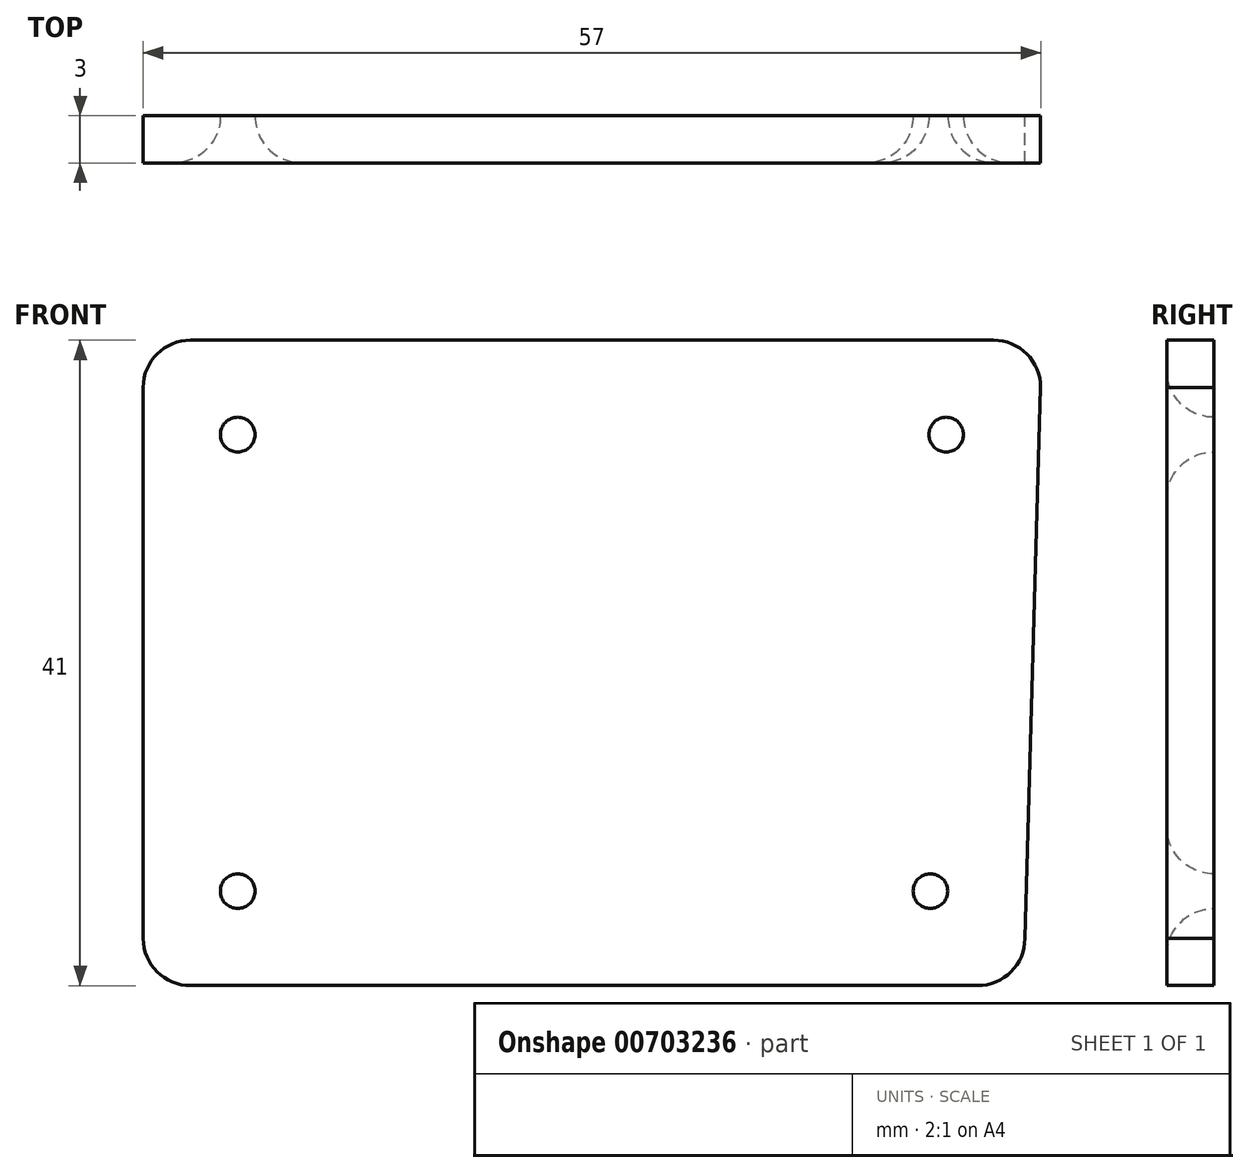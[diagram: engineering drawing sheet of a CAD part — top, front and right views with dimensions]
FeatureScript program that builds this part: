
annotation { "Feature Type Name" : "Feature", "Feature Type Description" : "" }
export const myFeature = defineFeature(function(context is Context, id is Id, definition is map)
    precondition{}
    {
        {
            var Q0;
            Q0=qCreatedBy(makeId("Front.planeOp"),FACE);
            var sketch = newSketch(context, id + "F0", { "sketchPlane" : qUnion([Q0])});
            skLineSegment(sketch, "E0", {"start": v(-25.48, -6.75) * mm, "end": v(-21.93, -6.75) * mm});
            skLineSegment(sketch, "E1", {"start": v(-21.93, -6.75) * mm, "end": v(-21.93, -4.75) * mm});
            skLineSegment(sketch, "E2", {"start": v(-21.93, -4.75) * mm, "end": v(-25.48, -4.75) * mm});
            skLineSegment(sketch, "E3", {"start": v(-25.48, -4.75) * mm, "end": v(-25.48, -2.75) * mm});
            skLineSegment(sketch, "E4", {"start": v(-25.48, -2.75) * mm, "end": v(-21.8, -2.75) * mm});
            skLineSegment(sketch, "E5", {"start": v(-21.8, -2.75) * mm, "end": v(-21.8, -0.75) * mm});
            skLineSegment(sketch, "E6", {"start": v(-21.8, -0.75) * mm, "end": v(-25.48, -0.75) * mm});
            skLineSegment(sketch, "E7", {"start": v(24.52, -0.75) * mm, "end": v(20.83, -0.75) * mm});
            skLineSegment(sketch, "E8", {"start": v(20.83, -0.75) * mm, "end": v(20.83, -2.75) * mm});
            skLineSegment(sketch, "E9", {"start": v(20.83, -2.75) * mm, "end": v(24.52, -2.75) * mm});
            skLineSegment(sketch, "E10", {"start": v(24.52, -2.75) * mm, "end": v(24.52, -4.75) * mm});
            skLineSegment(sketch, "E11", {"start": v(24.52, -4.75) * mm, "end": v(20.8, -4.75) * mm});
            skLineSegment(sketch, "E12", {"start": v(20.8, -4.75) * mm, "end": v(20.8, -6.75) * mm});
            skLineSegment(sketch, "E13", {"start": v(20.8, -6.75) * mm, "end": v(24.52, -6.75) * mm});
            skLineSegment(sketch, "E14", {"start": v(24.52, -6.75) * mm, "end": v(24.52, -14.75) * mm});
            skLineSegment(sketch, "E15.bottom", {"start": v(-25.48, 20.25) * mm, "end": v(-19.48, 20.25) * mm});
            skLineSegment(sketch, "E15.top", {"start": v(-25.48, 14.25) * mm, "end": v(-19.48, 14.25) * mm});
            skLineSegment(sketch, "E15.left", {"start": v(-25.48, 20.25) * mm, "end": v(-25.48, 14.25) * mm});
            skLineSegment(sketch, "E15.right", {"start": v(-19.48, 20.25) * mm, "end": v(-19.48, 14.25) * mm});
            skLineSegment(sketch, "E16.bottom", {"start": v(25.52, 20.25) * mm, "end": v(19.52, 20.25) * mm});
            skLineSegment(sketch, "E16.top", {"start": v(25.52, 14.25) * mm, "end": v(19.52, 14.25) * mm});
            skLineSegment(sketch, "E16.left", {"start": v(25.52, 20.25) * mm, "end": v(25.52, 14.25) * mm});
            skLineSegment(sketch, "E16.right", {"start": v(19.52, 20.25) * mm, "end": v(19.52, 14.25) * mm});
            skLineSegment(sketch, "E17.bottom", {"start": v(24.52, -14.75) * mm, "end": v(18.52, -14.75) * mm});
            skLineSegment(sketch, "E17.top", {"start": v(24.52, -8.75) * mm, "end": v(18.52, -8.75) * mm});
            skLineSegment(sketch, "E17.left", {"start": v(24.52, -14.75) * mm, "end": v(24.52, -8.75) * mm});
            skLineSegment(sketch, "E17.right", {"start": v(18.52, -14.75) * mm, "end": v(18.52, -8.75) * mm});
            skLineSegment(sketch, "E18.bottom", {"start": v(-25.48, -14.75) * mm, "end": v(-19.48, -14.75) * mm});
            skLineSegment(sketch, "E18.top", {"start": v(-25.48, -8.75) * mm, "end": v(-19.48, -8.75) * mm});
            skLineSegment(sketch, "E18.left", {"start": v(-25.48, -14.75) * mm, "end": v(-25.48, -8.75) * mm});
            skLineSegment(sketch, "E18.right", {"start": v(-19.48, -14.75) * mm, "end": v(-19.48, -8.75) * mm});
            skLineSegment(sketch, "E19.bottom", {"start": v(-25.48, -14.75) * mm, "end": v(25.52, -14.75) * mm});
            skLineSegment(sketch, "E19.top", {"start": v(-25.48, 20.25) * mm, "end": v(25.52, 20.25) * mm});
            skLineSegment(sketch, "E19.left", {"start": v(-25.48, -14.75) * mm, "end": v(-25.48, 20.25) * mm});
            skLineSegment(sketch, "E19.right", {"start": v(25.52, -14.75) * mm, "end": v(25.52, 20.25) * mm});
            skLineSegment(sketch, "E20.top", {"start": v(-25.48, -0.75) * mm, "end": v(-21.8, -0.75) * mm});
            skLineSegment(sketch, "E20.left", {"start": v(-25.48, -2.75) * mm, "end": v(-25.48, -0.75) * mm});
            skLineSegment(sketch, "E21.top", {"start": v(20.83, -0.75) * mm, "end": v(24.52, -0.75) * mm});
            skLineSegment(sketch, "E21.left", {"start": v(20.83, -2.75) * mm, "end": v(20.83, -0.75) * mm});
            skLineSegment(sketch, "E21.right", {"start": v(24.52, -2.75) * mm, "end": v(24.52, -0.75) * mm});
            skArc(sketch, "E22", {"start": v(-25.48, 23.25) * mm, "mid": v(-27.6, 22.38) * mm, "end": v(-28.48, 20.25) * mm});
            skArc(sketch, "E23", {"start": v(-25.48, -17.75) * mm, "mid": v(-27.6, -16.87) * mm, "end": v(-28.48, -14.75) * mm});
            skArc(sketch, "E24", {"start": v(24.52, -17.75) * mm, "mid": v(26.64, -16.87) * mm, "end": v(27.52, -14.75) * mm});
            skArc(sketch, "E25", {"start": v(25.52, 23.25) * mm, "mid": v(27.64, 22.38) * mm, "end": v(28.52, 20.25) * mm});
            skLineSegment(sketch, "E26", {"start": v(-28.48, -14.75) * mm, "end": v(-28.48, 20.25) * mm});
            skLineSegment(sketch, "E27", {"start": v(27.52, -14.75) * mm, "end": v(28.52, 20.25) * mm});
            skLineSegment(sketch, "E28", {"start": v(-25.48, -17.75) * mm, "end": v(24.52, -17.75) * mm});
            skLineSegment(sketch, "E29", {"start": v(25.52, 23.25) * mm, "end": v(-25.48, 23.25) * mm});
            skCircle(sketch, "E30", {"center": v(-22.48, -11.75) * mm, "radius": 1.1 * mm});
            skPoint(sketch, "E30.centerSnap0", {"position": v(-19.48, -11.75) * mm});
            skPoint(sketch, "E30.centerSnap1", {"position": v(-22.48, -14.75) * mm});
            skCircle(sketch, "E31", {"center": v(-22.48, 17.25) * mm, "radius": 1.1 * mm});
            skPoint(sketch, "E31.centerSnap0", {"position": v(-19.48, 17.25) * mm});
            skPoint(sketch, "E31.centerSnap1", {"position": v(-22.48, 14.25) * mm});
            skCircle(sketch, "E32", {"center": v(22.52, 17.25) * mm, "radius": 1.1 * mm});
            skPoint(sketch, "E32.centerSnap0", {"position": v(19.52, 17.25) * mm});
            skPoint(sketch, "E32.centerSnap1", {"position": v(22.52, 14.25) * mm});
            skCircle(sketch, "E33", {"center": v(21.52, -11.75) * mm, "radius": 1.1 * mm});
            skPoint(sketch, "E33.centerSnap0", {"position": v(21.52, -8.75) * mm});
            skPoint(sketch, "E33.centerSnap1", {"position": v(18.52, -11.75) * mm});
            skSolve(sketch);
        }
        {
            var Q0;
            Q0=makeQuery(id+"F0.imprint","IMPRINT",FACE,{"disambiguationData":[TD([[makeQuery(id+"F0.imprint","IMPRINT",EDGE,{"derivedFrom":sQuery(id+"F0.wireOp",EDGE,"E16.bottom")}),1.0]])]});
            var Q1;
            {var subQ2=sQuery(id+"F0.wireOp",EDGE,"E3");Q1=makeQuery(id+"F0.imprint","IMPRINT",FACE,{"disambiguationData":[TD([[makeQuery(id+"F0.imprint","IMPRINT",EDGE,{"derivedFrom":subQ2}),1.0]])]});}
            var Q2;
            Q2=makeQuery(id+"F0.imprint","IMPRINT",FACE,{"disambiguationData":[TD([[makeQuery(id+"F0.imprint","IMPRINT",EDGE,{"derivedFrom":sQuery(id+"F0.wireOp",EDGE,"E15.bottom")}),-1.0]])]});
            var Q3;
            {var subQ0=sQuery(id+"F0.wireOp",EDGE,"E0");Q3=makeQuery(id+"F0.imprint","IMPRINT",FACE,{"disambiguationData":[TD([[makeQuery(id+"F0.imprint","IMPRINT",EDGE,{"derivedFrom":subQ0}),1.0]])]});}
            var Q4;
            {var subQ9=sQuery(id+"F0.wireOp",EDGE,"E0");Q4=makeQuery(id+"F0.imprint","IMPRINT",FACE,{"disambiguationData":[TD([[makeQuery(id+"F0.imprint","IMPRINT",EDGE,{"derivedFrom":subQ9}),-1.0]])]});}
            var Q5;
            {var subQ0=sQuery(id+"F0.wireOp",EDGE,"E4");Q5=makeQuery(id+"F0.imprint","IMPRINT",FACE,{"disambiguationData":[TD([[makeQuery(id+"F0.imprint","IMPRINT",EDGE,{"derivedFrom":subQ0}),1.0]])]});}
            var Q6;
            Q6=makeQuery(id+"F0.imprint","IMPRINT",FACE,{"disambiguationData":[TD([[makeQuery(id+"F0.imprint","IMPRINT",EDGE,{"derivedFrom":sQuery(id+"F0.wireOp",EDGE,"E7")}),1.0]])]});
            var Q7;
            Q7=makeQuery(id+"F0.imprint","IMPRINT",FACE,{"disambiguationData":[TD([[makeQuery(id+"F0.imprint","IMPRINT",EDGE,{"derivedFrom":sQuery(id+"F0.wireOp",EDGE,"E18.bottom")}),1.0]])]});
            var Q8;
            {var subQ0=sQuery(id+"F0.wireOp",EDGE,"E11");Q8=makeQuery(id+"F0.imprint","IMPRINT",FACE,{"disambiguationData":[TD([[makeQuery(id+"F0.imprint","IMPRINT",EDGE,{"derivedFrom":subQ0}),1.0]])]});}
            var Q9;
            {var subQ2=sQuery(id+"F0.wireOp",EDGE,"E17.bottom");Q9=makeQuery(id+"F0.imprint","IMPRINT",FACE,{"disambiguationData":[TD([[makeQuery(id+"F0.imprint","IMPRINT",EDGE,{"derivedFrom":subQ2}),-1.0]])]});}
            extrude(context, id + "F1", {"entities" : qUnion([Q0, Q1, Q2, Q3, Q4, Q5, Q6, Q7, Q8, Q9]), "depth" : 3 * mm, "offsetDistance" : 25 * mm});
        }
        {
            var Q0;
            Q0=makeQuery(id+"F1.opExtrude","CAP_EDGE",EDGE,{"disambiguationData":[OSD([sQuery(id+"F0.wireOp",EDGE,"E30")])],"isStart":false});
            var Q1;
            Q1=makeQuery(id+"F1.opExtrude","CAP_EDGE",EDGE,{"disambiguationData":[OSD([sQuery(id+"F0.wireOp",EDGE,"E31")])],"isStart":false});
            var Q2;
            Q2=makeQuery(id+"F1.opExtrude","CAP_EDGE",EDGE,{"disambiguationData":[OSD([sQuery(id+"F0.wireOp",EDGE,"E32")])],"isStart":false});
            var Q3;
            Q3=makeQuery(id+"F1.opExtrude","CAP_EDGE",EDGE,{"disambiguationData":[OSD([sQuery(id+"F0.wireOp",EDGE,"E33")])],"isStart":false});
            fillet(context, id + "F2", {"entities" : qUnion([Q0, Q1, Q2, Q3]), "radius" : 3 * mm, "tangentPropagation" : true, "allowEdgeOverflow" : false});
        }
    });
